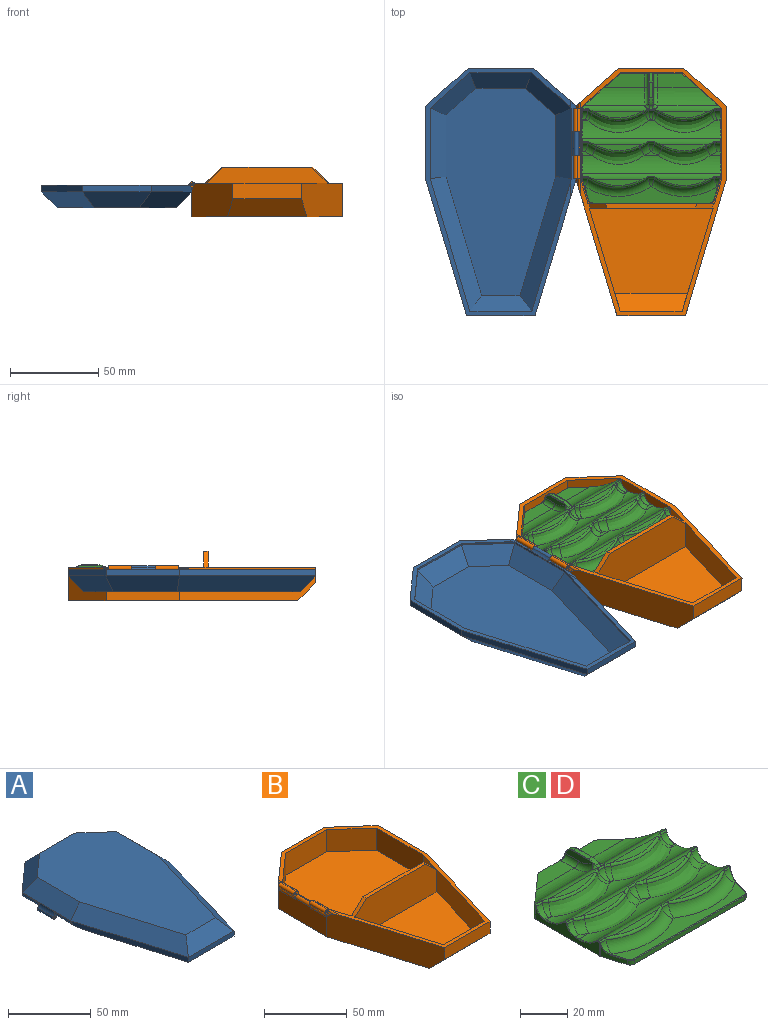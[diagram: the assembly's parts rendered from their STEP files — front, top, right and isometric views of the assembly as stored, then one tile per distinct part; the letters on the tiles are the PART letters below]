
ASSEMBLY  parts=4 mates=3
PART A: 45 faces, bbox 89.1x142.7x17.2 mm
  f0: plane 0.12x0mm, normal (0,1,0), area 0mm2, adj f8,f42
  f1: plane 0.12x0mm, normal (0,-1,0), area 0mm2, adj f8,f42
  f2: cylinder r=1.42mm len=13.33mm, axis (0,-1,0), area 61.4mm2, adj f4,f40,f41,f42
  f3: cylinder r=0.64mm len=13.33mm, axis (0,-1,0), area 53.2mm2, adj f40,f41
  f4: cylinder r=5.08mm len=13.33mm, axis (0,1,0), area 26.1mm2, adj f2,f5,f40,f41
  f5: plane 40x1.11mm, normal (1,0,0), area 43.4mm2, adj f4,f16,f22,f27,f40,f41,f43,f44
  f6: plane 140.08x81.78mm, normal (0,0,-1), area 825.5mm2, adj f7,f9,f10,f11,f12,f13,f14,f16
  f7: plane 24.08x21.4mm, normal (-0.66,0.75,0), area 115.7mm2, adj f6,f8,f14,f35,f44
  f8: plane 41.51x0.35mm, normal (-1,0,0), area 12.9mm2, adj f0,f1,f7,f9,f37,f42,f43,f44
  f9: plane 79.74x25.73mm, normal (-0.96,-0.29,0), area 289.2mm2, adj f6,f8,f10,f39,f43
  f10: plane 38.78x3.65mm, normal (0,-1,0), area 141.5mm2, adj f6,f9,f11,f38
  f11: plane 77.17x23.15mm, normal (0.96,-0.29,0), area 294.1mm2, adj f6,f10,f12,f36
  f12: plane 41.51x3.65mm, normal (1,0,0), area 151.5mm2, adj f6,f11,f13,f34
  f13: plane 24.07x21.4mm, normal (0.66,0.75,0), area 117.6mm2, adj f6,f12,f14,f32
  f14: plane 36.93x3.65mm, normal (0,1,0), area 134.8mm2, adj f6,f7,f13,f33
  f15: plane 122.3x67.3mm, normal (0,0,1), area 6472mm2, adj f32,f33,f34,f35,f36,f37,f38,f39
  f16: plane 22.64x20.14mm, normal (0.66,-0.75,0), area 33.4mm2, adj f5,f6,f17,f25,f44
  f17: plane 35x1.11mm, normal (0,-1,0), area 38.9mm2, adj f6,f16,f18,f24
  f18: plane 22.5x20mm, normal (-0.66,-0.75,0), area 33.4mm2, adj f6,f17,f19,f26
  f19: plane 40x1.11mm, normal (-1,0,0), area 44.4mm2, adj f6,f18,f20,f28
  f20: plane 75x22.5mm, normal (-0.96,0.29,0), area 86.9mm2, adj f6,f19,f21,f30
  f21: plane 35x1.11mm, normal (0,1,0), area 38.9mm2, adj f6,f20,f22,f31
  f22: plane 75.35x22.85mm, normal (0.96,0.29,0), area 86.9mm2, adj f5,f6,f21,f29,f43
  f23: plane 117.22x62.22mm, normal (0,0,-1), area 5673.4mm2, adj f24,f25,f26,f27,f28,f29,f30,f31
  f24: plane 35x8.89mm, normal (0,-0.71,-0.71), area 397.5mm2, adj f17,f23,f25,f26
  f25: plane 25.88x23.99mm, normal (0.47,-0.53,-0.71), area 332.1mm2, adj f16,f23,f24,f27
  f26: plane 25.88x23.99mm, normal (-0.47,-0.53,-0.71), area 332.1mm2, adj f18,f23,f24,f28
  f27: plane 40x8.89mm, normal (0.71,0,-0.71), area 469.6mm2, adj f5,f23,f25,f29
  f28: plane 40x8.89mm, normal (-0.71,0,-0.71), area 469.6mm2, adj f19,f23,f26,f30
  f29: plane 76.3x29.11mm, normal (0.68,0.2,-0.71), area 934.7mm2, adj f22,f23,f27,f31
  f30: plane 76.3x29.11mm, normal (-0.68,0.2,-0.71), area 934.7mm2, adj f20,f23,f28,f31
  f31: plane 35x8.89mm, normal (0,0.71,-0.71), area 356.9mm2, adj f21,f23,f29,f30
  f32: plane 27.45x25.39mm, normal (0.47,0.53,0.71), area 358.6mm2, adj f13,f15,f33,f34
  f33: plane 36.93x8.89mm, normal (0,0.71,0.71), area 421.8mm2, adj f14,f15,f32,f35
  f34: plane 41.51x8.89mm, normal (0.71,0,0.71), area 488.6mm2, adj f12,f15,f32,f36
  f35: plane 27.45x25.39mm, normal (-0.47,0.53,0.71), area 358.6mm2, adj f7,f15,f33,f37
  f36: plane 78.47x29.76mm, normal (0.68,-0.2,0.71), area 963.1mm2, adj f11,f15,f34,f38
  f37: plane 41.51x8.89mm, normal (-0.71,0,0.71), area 488.6mm2, adj f8,f15,f35,f39
  f38: plane 38.78x8.89mm, normal (0,-0.71,0.71), area 404.4mm2, adj f10,f15,f36,f39
  f39: plane 78.47x29.76mm, normal (-0.68,-0.2,0.71), area 963.1mm2, adj f9,f15,f37,f38
  f40: plane 5.49x4.09mm, normal (0,1,0), area 7.4mm2, adj f2,f3,f4,f5,f42,f44
  f41: plane 5.48x4.09mm, normal (0,-1,0), area 7.4mm2, adj f2,f3,f4,f5,f42,f43
  f42: cylinder r=5.08mm len=13.33mm, axis (0,-1,0), area 45.6mm2, adj f0,f1,f2,f8,f40,f41
  f43: bspline ~27.18x3.3mm, area 92mm2, adj f5,f6,f8,f9,f22,f41
  f44: bspline ~19.15x3.3mm, area 72.6mm2, adj f5,f6,f7,f8,f16,f40
PART B: 49 faces, bbox 86.5x140.1x27.9 mm
  f0: plane 58.42x17.53mm, normal (-0.96,0.29,0), area 943.3mm2, adj f22,f25,f31,f45,f47
  f1: plane 16.35x14.04mm, normal (0.96,0.29,0), area 239.7mm2, adj f8,f24,f31,f46
  f2: plane 5.48x3.85mm, normal (0,-1,0), area 6.5mm2, adj f3,f4,f5,f29,f32,f35,f36,f39
  f3: plane 41.51x14.93mm, normal (-1,0,0), area 599.5mm2, adj f2,f9,f10,f11,f26,f27,f28,f29
  f4: cylinder r=1.42mm len=13.33mm, axis (0,-1,0), area 54.6mm2, adj f2,f27,f29,f36
  f5: cylinder r=0.64mm len=13.33mm, axis (0,-1,0), area 53.2mm2, adj f2,f27
  f6: cylinder r=1.42mm len=13.33mm, axis (0,-1,0), area 54.6mm2, adj f9,f26,f28,f37
  f7: cylinder r=0.64mm len=13.33mm, axis (0,-1,0), area 53.2mm2, adj f9,f26
  f8: plane 40x16.35mm, normal (1,0,0), area 626.6mm2, adj f1,f17,f26,f27,f30,f31,f46
  f9: plane 5.48x3.85mm, normal (0,1,0), area 6.5mm2, adj f3,f6,f7,f28,f33,f34,f37,f38
  f10: plane 24.07x21.4mm, normal (-0.66,0.75,0), area 604.4mm2, adj f3,f16,f31,f33,f34,f38,f44
  f11: plane 77.17x23.15mm, normal (-0.96,-0.29,0), area 1457.3mm2, adj f3,f12,f31,f32,f35,f39,f44,f48
  f12: plane 38.78x8.73mm, normal (0,-1,0), area 338.5mm2, adj f11,f13,f31,f48
  f13: plane 77.17x23.15mm, normal (0.96,-0.29,0), area 1468mm2, adj f12,f14,f31,f44,f48
  f14: plane 41.51x18.89mm, normal (1,0,0), area 784.2mm2, adj f13,f15,f31,f44
  f15: plane 24.07x21.4mm, normal (0.66,0.75,0), area 608.5mm2, adj f14,f16,f31,f44
  f16: plane 36.93x18.89mm, normal (0,1,0), area 697.6mm2, adj f10,f15,f31,f44
  f17: plane 22.5x20mm, normal (0.66,-0.75,0), area 492.2mm2, adj f8,f18,f31,f46
  f18: plane 35x16.35mm, normal (0,-1,0), area 572.2mm2, adj f17,f19,f31,f46
  f19: plane 22.5x20mm, normal (-0.66,-0.75,0), area 492.2mm2, adj f18,f20,f31,f46
  f20: plane 40x16.35mm, normal (-1,0,0), area 654mm2, adj f19,f21,f31,f46
  f21: plane 16.35x14.04mm, normal (-0.96,0.29,0), area 239.7mm2, adj f20,f24,f31,f46
  f22: plane 35x6.19mm, normal (0,1,0), area 216.7mm2, adj f0,f23,f31,f47
  f23: plane 58.42x17.53mm, normal (0.96,0.29,0), area 943.3mm2, adj f22,f25,f31,f45,f47
  f24: plane 71.58x25.34mm, normal (0,1,0), area 1720.4mm2, adj f1,f21,f31,f41,f42,f43,f46
  f25: plane 70.05x25.34mm, normal (0,-1,0), area 1681.8mm2, adj f0,f23,f31,f41,f42,f43,f45
  f26: plane 5.48x3.96mm, normal (0,-1,0), area 9.4mm2, adj f3,f6,f7,f8,f28,f30,f31,f34
  f27: plane 5.48x3.96mm, normal (0,1,0), area 9.4mm2, adj f3,f4,f5,f8,f29,f30,f31,f35
  f28: cylinder r=5.08mm len=13.33mm, axis (0,-1,0), area 45.6mm2, adj f3,f6,f9,f26
  f29: cylinder r=5.08mm len=13.33mm, axis (0,-1,0), area 45.6mm2, adj f2,f3,f4,f27
  f30: plane 13.33x0.64mm, normal (0,0,1), area 8.5mm2, adj f8,f26,f27,f40
  f31: plane 140.08x82.62mm, normal (0,0,1), area 840.3mm2, adj f0,f1,f8,f10,f11,f12,f13,f14
  f32: cylinder r=5.08mm len=2.99mm, axis (0,-1,0), area 3.6mm2, adj f2,f3,f11,f39
  f33: cylinder r=5.08mm len=2.71mm, axis (0,1,0), area 3.9mm2, adj f3,f9,f10,f38
  f34: cylinder r=1.27mm len=16.66mm, axis (0,1,0), area 4.7mm2, adj f9,f10,f26,f31,f37,f38
  f35: cylinder r=1.27mm len=21.92mm, axis (0,1,0), area 10.2mm2, adj f2,f11,f27,f31,f36,f39
  f36: cylinder r=2.54mm len=13.33mm, axis (0,-1,0), area 22.6mm2, adj f2,f4,f27,f35
  f37: cylinder r=2.54mm len=13.33mm, axis (0,-1,0), area 22.6mm2, adj f6,f9,f26,f34
  f38: cylinder r=5.08mm len=2.27mm, axis (0,1,0), area 2.3mm2, adj f9,f10,f33,f34
  f39: cylinder r=5.08mm len=4.6mm, axis (0,-1,0), area 4.3mm2, adj f2,f11,f32,f35
  f40: cylinder r=1.91mm len=13.33mm, axis (0,-1,0), area 39.9mm2, adj f3,f26,f27,f30
  f41: plane 51.79x2.54mm, normal (0,0,1), area 129.6mm2, adj f24,f25,f42,f43
  f42: plane 10.15x8.99mm, normal (-0.68,-0.2,0.71), area 33.7mm2, adj f24,f25,f31,f41
  f43: plane 10.15x8.99mm, normal (0.68,-0.2,0.71), area 33.7mm2, adj f24,f25,f31,f41
  f44: plane 129.92x85.08mm, normal (0,0,-1), area 9191.4mm2, adj f3,f10,f11,f13,f14,f15,f16,f48
  f45: plane 70.05x48.26mm, normal (0,0,1), area 2682mm2, adj f0,f23,f25,f47
  f46: plane 80x74.04mm, normal (0,0,1), area 5414.1mm2, adj f1,f8,f17,f18,f19,f20,f21,f24
  f47: plane 41.1x10.16mm, normal (0,0.71,0.71), area 546.7mm2, adj f0,f22,f23,f45
  f48: plane 44.88x10.16mm, normal (0,-0.71,-0.71), area 601mm2, adj f11,f12,f13,f44
PART C: 152 faces, bbox 84.9x79x9.7 mm
  f0: plane 75.15x9.18mm, normal (0,0,1), area 389.9mm2, adj f27,f28,f29,f30,f31,f116,f119,f121
  f1: plane 12.35x5.29mm, normal (-0.96,-0.29,0), area 33.7mm2, adj f13,f82,f89,f125,f127
  f2: cylinder r=15.24mm len=34.12mm, axis (1,0,0), area 316.2mm2, adj f3,f14,f75,f148,f149
  f3: plane 22.81x8.29mm, normal (0,0,1), area 150.1mm2, adj f2,f14,f15,f85,f150,f151
  f4: plane 26.96x3.76mm, normal (0,0,1), area 67.3mm2, adj f53,f75
  f5: plane 26.91x3.64mm, normal (0,0,1), area 65.6mm2, adj f64,f65,f67,f74
  f6: plane 26.91x3.53mm, normal (0,0,1), area 64.1mm2, adj f72,f73
  f7: plane 3.32x0.83mm, normal (0,0,1), area 2.2mm2, adj f25,f42,f44,f94
  f8: plane 3.33x0.83mm, normal (0,0,1), area 1.6mm2, adj f25,f47,f48,f49
  f9: plane 5.69x2.1mm, normal (0,0,1), area 7.9mm2, adj f24,f32,f33,f126
  f10: plane 5.69x2.1mm, normal (0,0,1), area 7.9mm2, adj f24,f39,f40,f101
  f11: plane 3.32x0.83mm, normal (0,0,1), area 2.2mm2, adj f25,f41,f43,f113
  f12: plane 22.81x8.29mm, normal (0,0,1), area 150.1mm2, adj f15,f16,f26,f86,f141,f142
  f13: plane 78.73x73.79mm, normal (0,0,-1), area 5309.7mm2, adj f1,f14,f15,f16,f17,f18,f19,f81
  f14: plane 20.55x18.27mm, normal (-0.66,0.75,0), area 91.1mm2, adj f2,f3,f13,f75,f84,f85
  f15: plane 32.66x4.42mm, normal (0,1,0), area 88.9mm2, adj f3,f12,f13,f80,f85,f86,f141,f151
  f16: plane 20.55x18.27mm, normal (0.66,0.75,0), area 91.1mm2, adj f12,f13,f26,f75,f86,f87
  f17: plane 38.11x7.17mm, normal (1,0,0), area 142.3mm2, adj f13,f87,f88,f93,f94,f95,f97,f99
  f18: plane 12.35x5.29mm, normal (0.96,-0.29,0), area 33.7mm2, adj f13,f83,f88,f114,f116
  f19: plane 38.11x7.17mm, normal (-1,0,0), area 142.3mm2, adj f13,f84,f89,f111,f113,f115,f117,f122
  f20: plane 8.07x2.1mm, normal (0,0,1), area 8.8mm2, adj f24,f35,f36,f37
  f21: plane 26.96x3.76mm, normal (0,0,1), area 67.3mm2, adj f56,f75
  f22: plane 26.91x3.53mm, normal (0,0,1), area 64.1mm2, adj f69,f73
  f23: plane 26.91x3.64mm, normal (0,0,1), area 65.6mm2, adj f60,f61,f62,f74
  f24: cylinder r=15.24mm len=78.22mm, axis (1,0,0), area 659.6mm2, adj f9,f10,f20,f34,f38,f73,f102,f128
  f25: cylinder r=15.24mm len=78.22mm, axis (1,0,0), area 536.7mm2, adj f7,f8,f11,f45,f46,f74,f95,f115
  f26: cylinder r=15.24mm len=34.12mm, axis (1,0,0), area 316.2mm2, adj f12,f16,f75,f143,f144
  f27: cylinder r=5.08mm len=4.98mm, axis (1,0,0), area 14.4mm2, adj f0,f28,f68,f127,f129
  f28: torus R=33.65mm, axis (0,0,1), area 257.4mm2, adj f0,f27,f29,f69
  f29: cylinder r=5.08mm len=4.98mm, axis (1,0,0), area 15.3mm2, adj f0,f28,f30,f70
  f30: torus R=33.65mm, axis (0,0,1), area 257.4mm2, adj f0,f29,f31,f72
  f31: cylinder r=5.08mm len=4.98mm, axis (1,0,0), area 14.4mm2, adj f0,f30,f71,f112,f114
  f32: cylinder r=5.08mm len=4.98mm, axis (1,0,0), area 19.1mm2, adj f9,f33,f59,f124
  f33: torus R=33.65mm, axis (0,0,1), area 32.2mm2, adj f9,f32,f34,f60
  f34: bspline ~32.78x10.46mm, area 216.7mm2, adj f24,f33,f35,f61
  f35: torus R=33.65mm, axis (0,0,1), area 32.2mm2, adj f20,f34,f36,f62
  f36: cylinder r=5.08mm len=4.98mm, axis (1,0,0), area 15.3mm2, adj f20,f35,f37,f63
  f37: torus R=33.65mm, axis (0,0,1), area 32.2mm2, adj f20,f36,f38,f64
  f38: bspline ~32.78x10.46mm, area 216.7mm2, adj f24,f37,f39,f65
  f39: torus R=33.65mm, axis (0,0,1), area 32.2mm2, adj f10,f38,f40,f67
  f40: cylinder r=5.08mm len=4.98mm, axis (1,0,0), area 19.1mm2, adj f10,f39,f66,f100
  f41: cylinder r=5.08mm len=4.98mm, axis (1,0,0), area 20.1mm2, adj f11,f43,f52,f109,f111
  f42: cylinder r=5.08mm len=4.98mm, axis (1,0,0), area 20.1mm2, adj f7,f44,f50,f92,f93
  f43: torus R=33.65mm, axis (0,0,1), area 15.2mm2, adj f11,f41,f45,f54
  f44: torus R=33.65mm, axis (0,0,1), area 15.2mm2, adj f7,f42,f46,f51
  f45: bspline ~37.61x12.73mm, area 261.1mm2, adj f25,f43,f47,f56
  f46: bspline ~37.61x12.73mm, area 261.1mm2, adj f25,f44,f48,f53
  f47: torus R=33.65mm, axis (0,0,1), area 15.2mm2, adj f8,f45,f49,f58
  f48: torus R=33.65mm, axis (0,0,1), area 15.2mm2, adj f8,f46,f49,f55
  f49: cylinder r=5.08mm len=4.98mm, axis (1,0,0), area 15.3mm2, adj f8,f47,f48,f57
  f50: cylinder r=1.27mm len=3.69mm, axis (1,0,0), area 3.4mm2, adj f42,f51,f90,f91
  f51: torus R=27.43mm, axis (0,0,-1), area 3.9mm2, adj f44,f50,f53,f75,f90
  f52: cylinder r=1.27mm len=3.69mm, axis (1,0,0), area 3.4mm2, adj f41,f54,f105,f107
  f53: bspline ~32.79x6.3mm, area 48.7mm2, adj f4,f46,f51,f55,f75
  f54: torus R=27.43mm, axis (0,0,-1), area 3.9mm2, adj f43,f52,f56,f75,f105
  f55: torus R=27.43mm, axis (0,0,-1), area 3.9mm2, adj f48,f53,f57,f75
  f56: bspline ~32.79x6.3mm, area 48.7mm2, adj f21,f45,f54,f58,f75
  f57: cylinder r=1.27mm len=4.14mm, axis (1,0,0), area 4.2mm2, adj f49,f55,f58,f75
  f58: torus R=27.43mm, axis (0,0,-1), area 3.9mm2, adj f47,f56,f57,f75
  f59: cylinder r=1.27mm len=3.69mm, axis (1,0,0), area 3.4mm2, adj f32,f60,f118,f122
  f60: torus R=27.43mm, axis (0,0,-1), area 7.7mm2, adj f23,f33,f59,f61,f74,f118
  f61: bspline ~28.93x5.06mm, area 42.8mm2, adj f23,f34,f60,f62
  f62: torus R=27.43mm, axis (0,0,-1), area 7.8mm2, adj f23,f35,f61,f63,f74
  f63: cylinder r=1.27mm len=4.14mm, axis (1,0,0), area 4.2mm2, adj f36,f62,f64,f74
  f64: torus R=27.43mm, axis (0,0,-1), area 7.8mm2, adj f5,f37,f63,f65,f74
  f65: bspline ~28.93x5.06mm, area 42.8mm2, adj f5,f38,f64,f67
  f66: cylinder r=1.27mm len=3.69mm, axis (1,0,0), area 3.4mm2, adj f40,f67,f96,f99
  f67: torus R=27.43mm, axis (0,0,-1), area 7.7mm2, adj f5,f39,f65,f66,f74,f96
  f68: cylinder r=1.27mm len=3.69mm, axis (1,0,0), area 3.4mm2, adj f27,f69,f131,f132,f134
  f69: torus R=27.43mm, axis (0,0,-1), area 59.8mm2, adj f22,f28,f68,f70,f73,f131
  f70: cylinder r=1.27mm len=4.14mm, axis (1,0,0), area 4.2mm2, adj f29,f69,f72,f73
  f71: cylinder r=1.27mm len=3.69mm, axis (1,0,0), area 3.4mm2, adj f31,f72,f103,f108,f110
  f72: torus R=27.43mm, axis (0,0,-1), area 59.8mm2, adj f6,f30,f70,f71,f73,f103
  f73: cylinder r=5.08mm len=78.22mm, axis (1,0,0), area 262.4mm2, adj f6,f22,f24,f69,f70,f72,f103,f104
  f74: cylinder r=5.08mm len=78.22mm, axis (1,0,0), area 262.4mm2, adj f5,f23,f25,f60,f62,f63,f64,f67
  f75: cylinder r=5.08mm len=78.48mm, axis (1,0,0), area 246.4mm2, adj f2,f4,f14,f16,f21,f26,f51,f53
  f76: plane 16.21x3.56mm, normal (-1,0,0), area 44.7mm2, adj f138,f139,f140,f149,f150
  f77: plane 16.21x3.56mm, normal (1,0,0), area 44.7mm2, adj f135,f136,f137,f142,f143
  f78: plane 8.85x2.03mm, normal (0,0,1), area 18mm2, adj f79,f80,f136,f139
  f79: cylinder r=8.89mm len=4.47mm, axis (1,0,0), area 9.5mm2, adj f78,f135,f138,f146
  f80: cylinder r=5.08mm len=5.08mm, axis (-1,0,0), area 15.8mm2, adj f15,f78,f137,f140,f141,f151
  f81: plane 66.24x2.29mm, normal (0,-1,0), area 151.4mm2, adj f13,f82,f83,f121
  f82: cylinder r=2.54mm len=2.43mm, axis (0,0,1), area 7.4mm2, adj f1,f13,f81,f123
  f83: cylinder r=2.54mm len=2.43mm, axis (0,0,1), area 7.4mm2, adj f13,f18,f81,f119
  f84: cylinder r=2.54mm len=7.32mm, axis (0,0,1), area 15.1mm2, adj f13,f14,f19,f75,f107,f109
  f85: cylinder r=2.54mm len=2.54mm, axis (0,0,1), area 4.7mm2, adj f3,f13,f14,f15
  f86: cylinder r=2.54mm len=2.54mm, axis (0,0,1), area 4.7mm2, adj f12,f13,f15,f16
  f87: cylinder r=2.54mm len=7.32mm, axis (0,0,1), area 15.1mm2, adj f13,f16,f17,f75,f91,f92
  f88: cylinder r=2.54mm len=7.01mm, axis (0,0,1), area 4.6mm2, adj f13,f17,f18,f110,f112
  f89: cylinder r=2.54mm len=7.01mm, axis (0,0,1), area 4.6mm2, adj f1,f13,f19,f129,f132
  f90: cylinder r=0.25mm len=3.81mm, axis (-1,0,0), area 0.8mm2, adj f50,f51,f75,f91
  f91: bspline ~1.25x1.18mm, area 0.4mm2, adj f50,f75,f87,f90,f92
  f92: bspline ~0.33x0.31mm, area 0mm2, adj f42,f87,f91,f93
  f93: torus R=5.33mm, axis (1,0,0), area 2.8mm2, adj f17,f42,f92,f94
  f94: cylinder r=0.25mm len=0.83mm, axis (0,1,0), area 0.3mm2, adj f7,f17,f93,f95
  f95: torus R=15.49mm, axis (1,0,0), area 4.4mm2, adj f17,f25,f94,f97
  f96: cylinder r=0.25mm len=3.69mm, axis (-1,0,0), area 0.8mm2, adj f66,f67,f74,f98
  f97: torus R=4.83mm, axis (1,0,0), area 0.9mm2, adj f17,f74,f95,f98
  f98: sphere r=0.25mm, area 0.1mm2, adj f96,f97,f99
  f99: torus R=1.02mm, axis (1,0,0), area 0.3mm2, adj f17,f66,f98,f100
  f100: torus R=5.33mm, axis (1,0,0), area 2.8mm2, adj f17,f40,f99,f101
  f101: cylinder r=0.25mm len=2.1mm, axis (0,1,0), area 0.8mm2, adj f10,f17,f100,f102
  f102: torus R=15.49mm, axis (1,0,0), area 4.4mm2, adj f17,f24,f101,f104
  f103: cylinder r=0.25mm len=3.69mm, axis (-1,0,0), area 0.8mm2, adj f71,f72,f73,f106
  f104: torus R=4.83mm, axis (1,0,0), area 0.9mm2, adj f17,f73,f102,f106
  f105: cylinder r=0.25mm len=3.81mm, axis (-1,0,0), area 0.8mm2, adj f52,f54,f75,f107
  f106: sphere r=0.25mm, area 0.1mm2, adj f103,f104,f108
  f107: bspline ~1.18x1.18mm, area 0.4mm2, adj f52,f75,f84,f105,f109
  f108: torus R=1.02mm, axis (1,0,0), area 0.1mm2, adj f17,f71,f106,f110
  f109: bspline ~0.32x0.31mm, area 0mm2, adj f41,f84,f107,f111
  f110: bspline ~0.91x0.54mm, area 0.2mm2, adj f71,f88,f108,f112
  f111: torus R=5.33mm, axis (-1,0,0), area 2.8mm2, adj f19,f41,f109,f113
  f112: bspline ~2.54x1.12mm, area 0.5mm2, adj f31,f88,f110,f114
  f113: cylinder r=0.25mm len=0.83mm, axis (0,-1,0), area 0.3mm2, adj f11,f19,f111,f115
  f114: bspline ~5.94x3.59mm, area 2.2mm2, adj f18,f31,f112,f116
  f115: torus R=15.49mm, axis (-1,0,0), area 4.4mm2, adj f19,f25,f113,f117
  f116: cylinder r=0.25mm len=7.62mm, axis (0.29,0.96,0), area 3.1mm2, adj f0,f18,f114,f119
  f117: torus R=4.83mm, axis (-1,0,0), area 0.9mm2, adj f19,f74,f115,f120
  f118: cylinder r=0.25mm len=3.69mm, axis (-1,0,0), area 0.8mm2, adj f59,f60,f74,f120
  f119: torus R=2.29mm, axis (0,0,1), area 1.2mm2, adj f0,f83,f116,f121
  f120: sphere r=0.25mm, area 0.1mm2, adj f117,f118,f122
  f121: cylinder r=0.25mm len=66.24mm, axis (1,0,0), area 26.4mm2, adj f0,f81,f119,f123
  f122: torus R=1.02mm, axis (-1,0,0), area 0.3mm2, adj f19,f59,f120,f124
  f123: torus R=2.29mm, axis (0,0,1), area 1.2mm2, adj f0,f82,f121,f125
  f124: torus R=5.33mm, axis (-1,0,0), area 2.8mm2, adj f19,f32,f122,f126
  f125: cylinder r=0.25mm len=7.62mm, axis (0.29,-0.96,0), area 3.1mm2, adj f0,f1,f123,f127
  f126: cylinder r=0.25mm len=2.1mm, axis (0,-1,0), area 0.8mm2, adj f9,f19,f124,f128
  f127: bspline ~5.94x3.59mm, area 2.2mm2, adj f1,f27,f125,f129
  f128: torus R=15.49mm, axis (-1,0,0), area 4.4mm2, adj f19,f24,f126,f130
  f129: bspline ~2.54x1.12mm, area 0.5mm2, adj f27,f89,f127,f132
  f130: torus R=4.83mm, axis (-1,0,0), area 0.9mm2, adj f19,f73,f128,f133
  f131: cylinder r=0.25mm len=3.69mm, axis (-1,0,0), area 0.8mm2, adj f68,f69,f73,f133
  f132: bspline ~0.88x0.67mm, area 0.2mm2, adj f68,f89,f129,f134
  f133: sphere r=0.25mm, area 0.1mm2, adj f130,f131,f134
  f134: torus R=1.02mm, axis (-1,0,0), area 0.1mm2, adj f19,f68,f132,f133
  f135: torus R=8.64mm, axis (-1,0,0), area 1.6mm2, adj f77,f79,f136,f144,f145
  f136: cylinder r=0.25mm len=8.85mm, axis (0,-1,0), area 3.5mm2, adj f77,f78,f135,f137
  f137: torus R=4.83mm, axis (-1,0,0), area 2.7mm2, adj f77,f80,f136,f141
  f138: torus R=8.64mm, axis (-1,0,0), area 1.6mm2, adj f76,f79,f139,f147,f148
  f139: cylinder r=0.25mm len=8.85mm, axis (0,1,0), area 3.5mm2, adj f76,f78,f138,f140
  f140: torus R=4.83mm, axis (-1,0,0), area 2.7mm2, adj f76,f80,f139,f151
  f141: bspline ~5.31x3.18mm, area 1.7mm2, adj f12,f15,f80,f137,f142
  f142: cylinder r=2.54mm len=7.87mm, axis (0,1,0), area 31.4mm2, adj f12,f77,f141,f143
  f143: torus R=12.7mm, axis (-1,0,0), area 40.9mm2, adj f26,f77,f142,f144
  f144: bspline ~2.55x1.95mm, area 0.2mm2, adj f26,f135,f143,f145
  f145: bspline ~4.04x2.93mm, area 6.3mm2, adj f75,f135,f144,f146
  f146: cylinder r=2.54mm len=2.03mm, axis (1,0,0), area 4.1mm2, adj f75,f79,f145,f147
  f147: bspline ~3.82x3.3mm, area 6.3mm2, adj f75,f138,f146,f148
  f148: bspline ~2.6x2.05mm, area 0.2mm2, adj f2,f138,f147,f149
  f149: torus R=12.7mm, axis (-1,0,0), area 40.9mm2, adj f2,f76,f148,f150
  f150: cylinder r=2.54mm len=7.87mm, axis (0,-1,0), area 31.4mm2, adj f3,f76,f149,f151
  f151: bspline ~5.26x3.14mm, area 1.7mm2, adj f3,f15,f80,f140,f150
PART D: same geometry as C
PLACE A rot(axis=(0,-1,0),180deg) t=(-22.79,26.95,-77.98)mm
PLACE B rot(axis=(0.71,0.21,-0.67),0deg) t=(62.29,26.95,-77.98)mm fixed
PLACE C rot(axis=(0.71,0.21,-0.67),0deg) t=(-26.35,27.38,-71.68)mm
PLACE D t=(-26.35,27.38,-80.52)mm
MATE slider C.f13 <-> B.f46  axis (0,0,-1) through (62.29,122.76,-71.68)mm
MATE revolute A.f2 <-> B.f4  axis (0,-1,0) through (19.75,115.28,-64.81)mm
MATE slider D.f13 <-> B.f46  axis (0,0,-1) through (62.29,122.76,-80.52)mm
